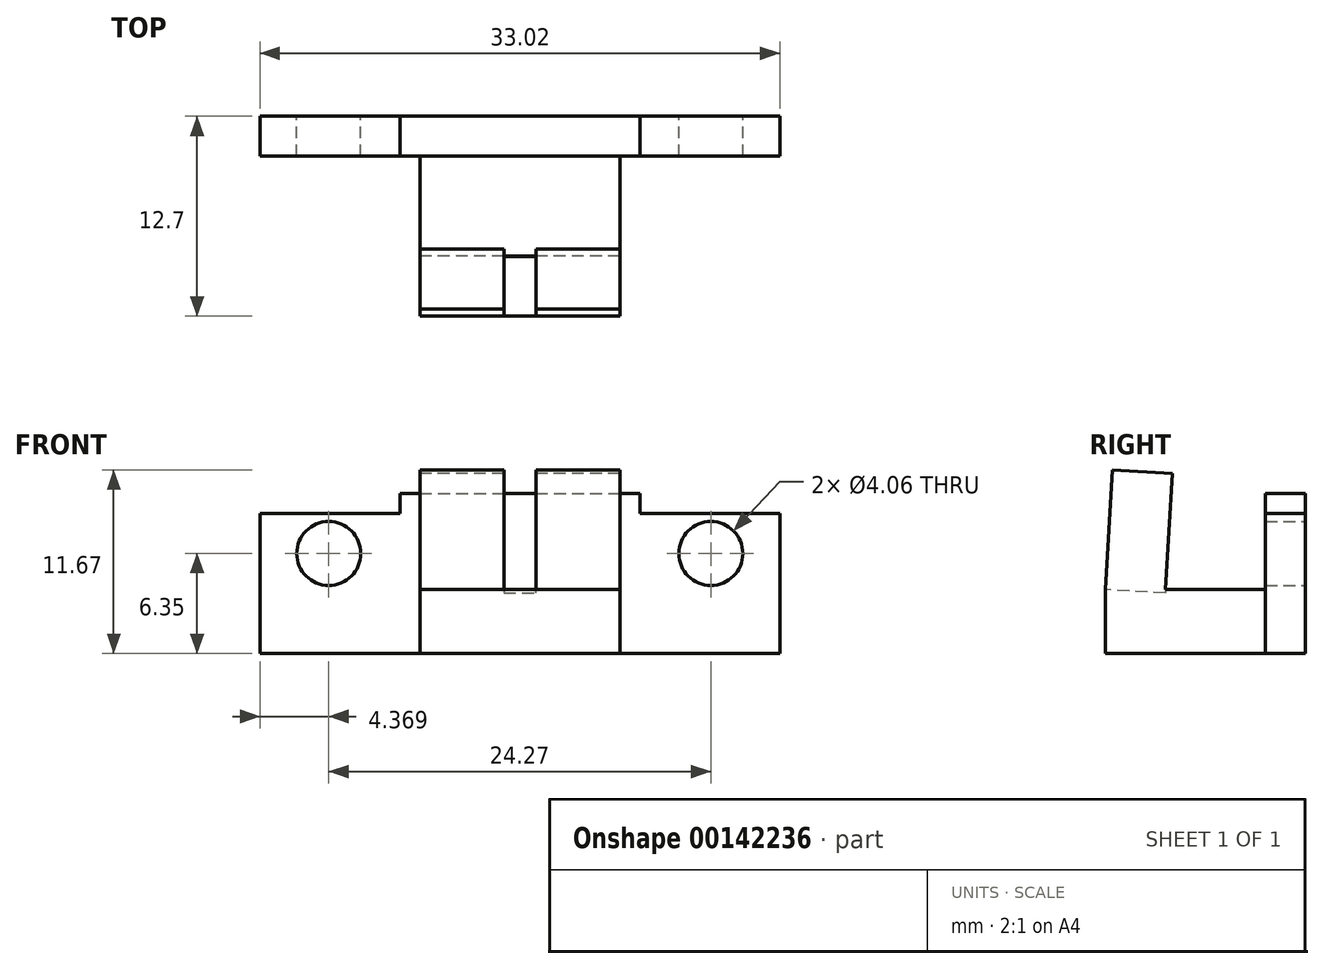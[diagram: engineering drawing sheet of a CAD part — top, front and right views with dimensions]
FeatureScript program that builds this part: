
annotation { "Feature Type Name" : "Feature", "Feature Type Description" : "" }
export const myFeature = defineFeature(function(context is Context, id is Id, definition is map)
    precondition{}
    {
        {
            var Q0;
            Q0=qCreatedBy(makeId("Front.planeOp"),FACE);
            var sketch = newSketch(context, id + "F0", { "sketchPlane" : qUnion([Q0])});
            skLineSegment(sketch, "E0.bottom", {"start": v(-7.62, 3.81) * mm, "end": v(7.62, 3.81) * mm});
            skLineSegment(sketch, "E0.top", {"start": v(-16.51, -6.35) * mm, "end": v(16.51, -6.35) * mm});
            skLineSegment(sketch, "E0.left", {"start": v(-16.51, 2.54) * mm, "end": v(-16.51, -6.35) * mm});
            skLineSegment(sketch, "E0.right", {"start": v(16.51, 2.54) * mm, "end": v(16.51, -6.35) * mm});
            skCircle(sketch, "E1", {"center": v(-12.14, 0) * mm, "radius": 2.03 * mm});
            skCircle(sketch, "E2", {"center": v(12.13, 0) * mm, "radius": 2.03 * mm});
            skLineSegment(sketch, "E3", {"start": v(-16.51, 2.54) * mm, "end": v(-7.62, 2.54) * mm});
            skLineSegment(sketch, "E4", {"start": v(-7.62, 2.54) * mm, "end": v(-7.62, 3.81) * mm});
            skLineSegment(sketch, "E5", {"start": v(16.51, 2.54) * mm, "end": v(7.62, 2.54) * mm});
            skLineSegment(sketch, "E6", {"start": v(7.62, 2.54) * mm, "end": v(7.62, 3.81) * mm});
            skSolve(sketch);
        }
        {
            var Q0;
            Q0=makeQuery(id+"F0.imprint","IMPRINT",FACE,{"disambiguationData":[TD([[makeQuery(id+"F0.imprint","IMPRINT",EDGE,{"derivedFrom":sQuery(id+"F0.wireOp",EDGE,"E0.bottom")}),-1.0]])]});
            extrude(context, id + "F1", {"entities" : qUnion([Q0]), "depth" : 2.54 * mm});
        }
        {
            var Q0;
            Q0=makeQuery(id+"F1.opExtrude","CAP_FACE",FACE,{"disambiguationData":[OSD([sQuery(id+"F0.wireOp",EDGE,"E0.bottom"),sQuery(id+"F0.wireOp",EDGE,"E0.top"),sQuery(id+"F0.wireOp",EDGE,"E0.left"),sQuery(id+"F0.wireOp",EDGE,"E0.right"),sQuery(id+"F0.wireOp",EDGE,"E1"),sQuery(id+"F0.wireOp",EDGE,"E2"),sQuery(id+"F0.wireOp",EDGE,"E3"),sQuery(id+"F0.wireOp",EDGE,"E4"),sQuery(id+"F0.wireOp",EDGE,"E5"),sQuery(id+"F0.wireOp",EDGE,"E6")])],"isStart":false});
            var sketch = newSketch(context, id + "F2", { "sketchPlane" : qUnion([Q0])});
            skLineSegment(sketch, "E7.bottom", {"start": v(-6.35, -6.35) * mm, "end": v(6.35, -6.35) * mm});
            skLineSegment(sketch, "E7.top", {"start": v(-6.35, -2.29) * mm, "end": v(6.35, -2.29) * mm});
            skLineSegment(sketch, "E7.left", {"start": v(-6.35, -6.35) * mm, "end": v(-6.35, -2.29) * mm});
            skLineSegment(sketch, "E7.right", {"start": v(6.35, -6.35) * mm, "end": v(6.35, -2.29) * mm});
            skSolve(sketch);
        }
        {
            var Q0;
            Q0=makeQuery(id+"F2.imprint","IMPRINT",FACE,{"disambiguationData":[TD([[makeQuery(id+"F2.imprint","IMPRINT",EDGE,{"derivedFrom":sQuery(id+"F2.wireOp",EDGE,"E7.bottom")}),1.0]])]});
            extrude(context, id + "F3", {"entities" : qUnion([Q0]), "operationType" : NewBodyOperationType.ADD, "depth" : 10.16 * mm});
        }
        {
            var Q0;
            Q0=makeQuery(id+"F3.opExtrude","SWEPT_FACE",FACE,{"disambiguationData":[OSD([sQuery(id+"F2.wireOp",EDGE,"E7.left")])]});
            var sketch = newSketch(context, id + "F4", { "sketchPlane" : qUnion([Q0])});
            skLineSegment(sketch, "E8", {"start": v(12.7, -2.29) * mm, "end": v(12.24, 5.32) * mm});
            skLineSegment(sketch, "E9", {"start": v(12.24, 5.32) * mm, "end": v(8.44, 5.1) * mm});
            skLineSegment(sketch, "E10", {"start": v(8.44, 5.1) * mm, "end": v(8.88, -2.29) * mm});
            skSolve(sketch);
        }
        {
            var Q0;
            {var subQ0=sQuery(id+"F4.wireOp",EDGE,"E8");Q0=makeQuery(id+"F4.imprint","IMPRINT",FACE,{"disambiguationData":[TD([[makeQuery(id+"F4.imprint","IMPRINT",EDGE,{"derivedFrom":subQ0}),1.0]])]});}
            extrude(context, id + "F5", {"entities" : qUnion([Q0]), "operationType" : NewBodyOperationType.ADD, "oppositeDirection" : true, "depth" : 12.7 * mm});
        }
        {
            var Q0;
            Q0=makeQuery(id+"F5.opExtrude","SWEPT_FACE",FACE,{"disambiguationData":[OSD([sQuery(id+"F4.wireOp",EDGE,"E8")])]});
            var sketch = newSketch(context, id + "F6", { "sketchPlane" : qUnion([Q0])});
            skLineSegment(sketch, "E11", {"start": v(-1.02, 4.58) * mm, "end": v(-1.02, -6.03) * mm});
            skLineSegment(sketch, "E12", {"start": v(-1.02, -6.03) * mm, "end": v(0, -6.03) * mm});
            skLineSegment(sketch, "E13", {"start": v(0, -6.03) * mm, "end": v(1.02, -6.03) * mm});
            skPoint(sketch, "E13.endSnap0", {"position": v(-0.5, -6.03) * mm});
            skLineSegment(sketch, "E14", {"start": v(1.02, -6.03) * mm, "end": v(1.02, 4.58) * mm});
            skSolve(sketch);
        }
        {
            var Q0;
            {var subQ1=sQuery(id+"F6.wireOp",EDGE,"E11");Q0=makeQuery(id+"F6.imprint","IMPRINT",FACE,{"disambiguationData":[TD([[makeQuery(id+"F6.imprint","IMPRINT",EDGE,{"derivedFrom":subQ1}),1.0]])]});}
            extrude(context, id + "F7", {"entities" : qUnion([Q0]), "operationType" : NewBodyOperationType.REMOVE, "oppositeDirection" : true, "depth" : 3.8 * mm});
        }
    });
